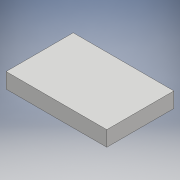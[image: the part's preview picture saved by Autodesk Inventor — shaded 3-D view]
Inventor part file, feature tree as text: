
AUTODESK INVENTOR PART (.ipt)
format: ipt  version: 2018 (Build 220112000, 112)  size: 90,112 bytes
history: native  units: mm
features: other x1, extrude x1, sketch x1
ambient origin geometry x8: Origin, YZ Plane, XZ Plane, XY Plane, X Axis, Y Axis, Z Axis, Center Point
bodies: Body1 (feature_tree)
feature tree (3):
  other  "Sólido1"
  extrude  "Extrusão1"  Depth=70.0mm
  sketch  "Esboço1"  dims[d0=105.0mm d1=70.0mm d2=15.88mm d3=0.0mm]
